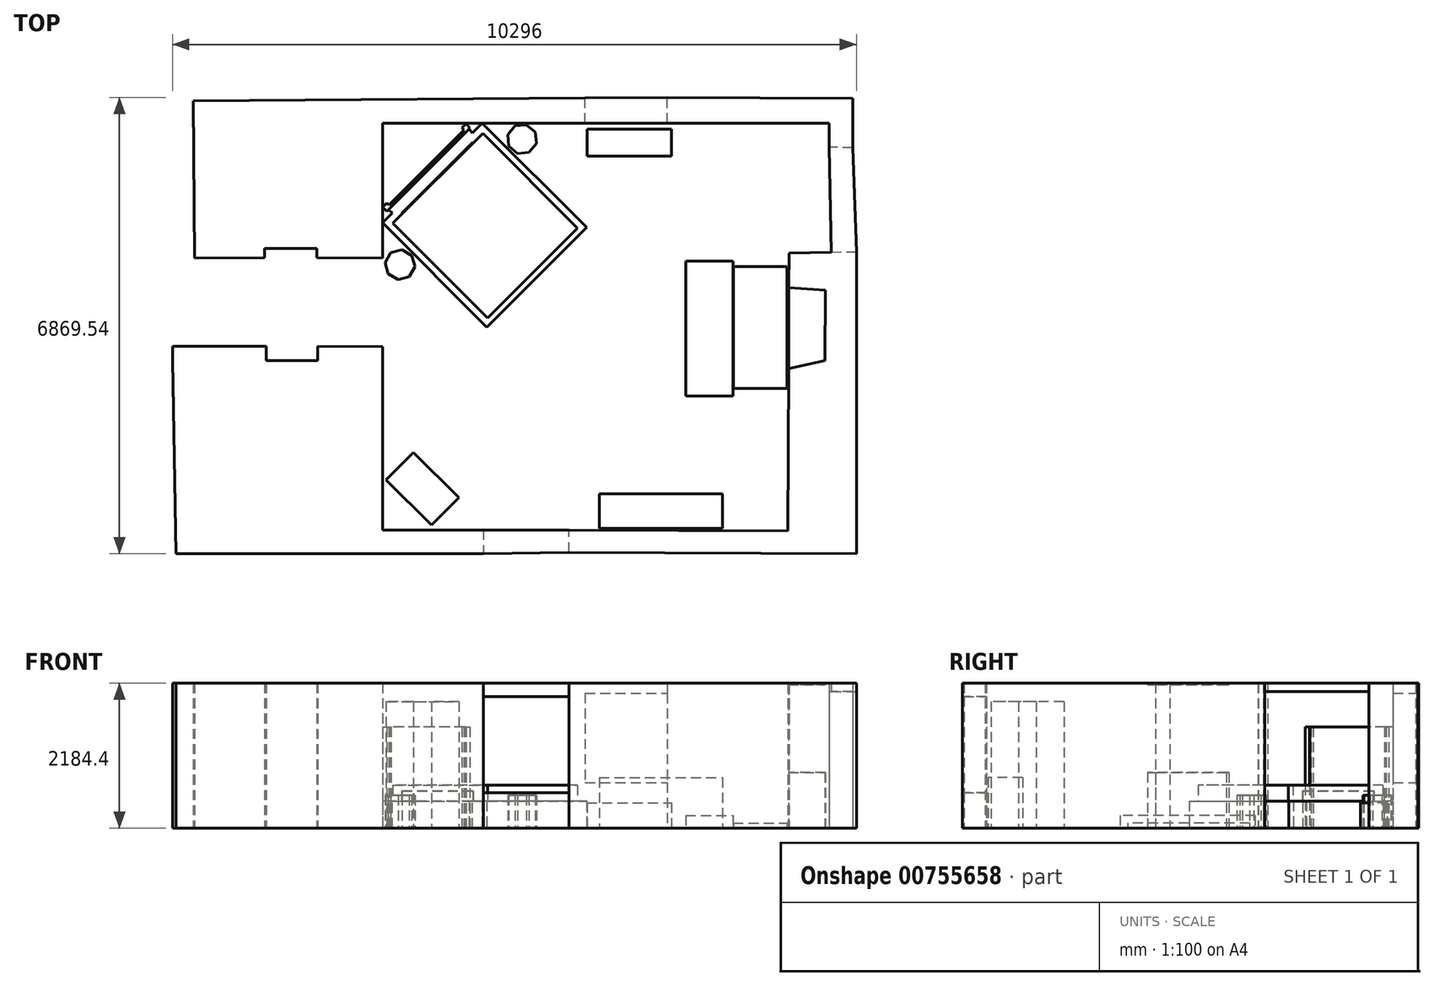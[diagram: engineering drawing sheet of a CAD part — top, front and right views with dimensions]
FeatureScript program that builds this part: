
annotation { "Feature Type Name" : "Feature", "Feature Type Description" : "" }
export const myFeature = defineFeature(function(context is Context, id is Id, definition is map)
    precondition{}
    {
        {
            var Q0;
            Q0=qCreatedBy(makeId("Top.planeOp"),FACE);
            var sketch = newSketch(context, id + "F0", { "sketchPlane" : qUnion([Q0])});
            skLineSegment(sketch, "E0", {"start": v(0, 0) * mm, "end": v(0, -2032) * mm});
            skLineSegment(sketch, "E1", {"start": v(0, 0) * mm, "end": v(3033.71, 0) * mm});
            skLineSegment(sketch, "E2", {"start": v(4288.2, 0) * mm, "end": v(6068.64, 0) * mm});
            skLineSegment(sketch, "E3", {"start": v(0, -2032) * mm, "end": v(0, -6124.58) * mm});
            skPoint(sketch, "E4", {"position": v(0, -1397) * mm});
            skPoint(sketch, "E5", {"position": v(1397, 0) * mm});
            skLineSegment(sketch, "E6", {"start": v(0, -1397) * mm, "end": v(1397, 0) * mm});
            skPoint(sketch, "E7", {"position": v(698.5, -698.5) * mm});
            skLineSegment(sketch, "E8", {"start": v(698.5, -698.5) * mm, "end": v(4954.33, -4954.33) * mm, "construction": true});
            skPoint(sketch, "E9", {"position": v(2270.04, -2270.04) * mm});
            skLineSegment(sketch, "E10", {"start": v(2270.04, -2270.04) * mm, "end": v(1520.2, -3019.9) * mm});
            skPoint(sketch, "E11", {"position": v(1663.88, -2876.21) * mm});
            skLineSegment(sketch, "E12", {"start": v(1571.54, -3071.25) * mm, "end": v(0, -1499.7) * mm});
            skLineSegment(sketch, "E13", {"start": v(1663.88, -2876.21) * mm, "end": v(92.33, -1304.67) * mm});
            skLineSegment(sketch, "E14", {"start": v(0, -1499.7) * mm, "end": v(749.85, -749.85) * mm});
            skLineSegment(sketch, "E15", {"start": v(1571.54, -3071.25) * mm, "end": v(2321.4, -2321.4) * mm});
            skLineSegment(sketch, "E16.MirrorCS", {"start": v(1397, 0) * mm, "end": v(0, -1397) * mm});
            skLineSegment(sketch, "E17.MirrorCS", {"start": v(2876.21, -1663.88) * mm, "end": v(1304.67, -92.33) * mm});
            skLineSegment(sketch, "E18.MirrorCS", {"start": v(2270.04, -2270.04) * mm, "end": v(3019.9, -1520.2) * mm});
            skLineSegment(sketch, "E19.MirrorCS", {"start": v(3071.25, -1571.54) * mm, "end": v(1499.7, 0) * mm});
            skLineSegment(sketch, "E20.MirrorCS", {"start": v(3071.25, -1571.54) * mm, "end": v(2321.4, -2321.4) * mm});
            skLineSegment(sketch, "E21.MirrorCS", {"start": v(1499.7, 0) * mm, "end": v(749.85, -749.85) * mm});
            skSolve(sketch);
        }
        {
            var Q0;
            {var subQ1=sQuery(id+"F0.wireOp",EDGE,"E16.MirrorCS");var subQ7=sQuery(id+"F0.wireOp",EDGE,"E13");var subQ9=makeQuery(id+"F0.imprint","INTERSECT",VERTEX,{"derivedFrom":[subQ7,subQ1]});Q0=makeQuery(id+"F0.imprint","IMPRINT",FACE,{"disambiguationData":[TD([[makeQuery(id+"F0.imprint","IMPRINT",EDGE,{"disambiguationData":[TD([[subQ9,1.0]])],"derivedFrom":subQ7}),-1.0]])]});}
            var Q1;
            {var subQ0=sQuery(id+"F0.wireOp",EDGE,"E18.MirrorCS");var subQ9=sQuery(id+"F0.wireOp",EDGE,"E10");var subQ11=makeQuery(id+"F0.imprint","INTERSECT",VERTEX,{"derivedFrom":[subQ9,subQ0]});Q1=makeQuery(id+"F0.imprint","IMPRINT",FACE,{"disambiguationData":[TD([[makeQuery(id+"F0.imprint","IMPRINT",EDGE,{"disambiguationData":[TD([[subQ11,-1.0]])],"derivedFrom":subQ9}),-1.0]])]});}
            extrude(context, id + "F1", {"entities" : qUnion([Q0, Q1]), "depth" : 406.4 * mm, "offsetDistance" : 25.4 * mm});
        }
        {
            var Q0;
            {var subQ0=sQuery(id+"F0.wireOp",EDGE,"E18.MirrorCS");var subQ9=sQuery(id+"F0.wireOp",EDGE,"E10");var subQ11=makeQuery(id+"F0.imprint","INTERSECT",VERTEX,{"derivedFrom":[subQ9,subQ0]});Q0=makeQuery(id+"F0.imprint","IMPRINT",FACE,{"disambiguationData":[TD([[makeQuery(id+"F0.imprint","IMPRINT",EDGE,{"disambiguationData":[TD([[subQ11,-1.0]])],"derivedFrom":subQ9}),-1.0]])]});}
            var Q1;
            {var subQ0=sQuery(id+"F0.wireOp",EDGE,"E12");var subQ1=sQuery(id+"F0.wireOp",EDGE,"E10");var subQ2=makeQuery(id+"F0.imprint","INTERSECT",VERTEX,{"derivedFrom":[subQ1,subQ0]});Q1=makeQuery(id+"F0.imprint","IMPRINT",FACE,{"disambiguationData":[TD([[makeQuery(id+"F0.imprint","IMPRINT",EDGE,{"disambiguationData":[TD([[subQ2,1.0]])],"derivedFrom":subQ1}),-1.0]])]});}
            var Q2;
            {var subQ0=sQuery(id+"F0.wireOp",EDGE,"E18.MirrorCS");var subQ1=sQuery(id+"F0.wireOp",EDGE,"E17.MirrorCS");var subQ2=makeQuery(id+"F0.imprint","INTERSECT",VERTEX,{"derivedFrom":[subQ1,subQ0]});Q2=makeQuery(id+"F0.imprint","IMPRINT",FACE,{"disambiguationData":[TD([[makeQuery(id+"F0.imprint","IMPRINT",EDGE,{"disambiguationData":[TD([[subQ2,-1.0]])],"derivedFrom":subQ1}),-1.0]])]});}
            var Q3;
            {var subQ0=sQuery(id+"F0.wireOp",EDGE,"E15");Q3=makeQuery(id+"F0.imprint","IMPRINT",FACE,{"disambiguationData":[TD([[makeQuery(id+"F0.imprint","IMPRINT",EDGE,{"derivedFrom":subQ0}),1.0]])]});}
            extrude(context, id + "F2", {"entities" : qUnion([Q0, Q1, Q2, Q3]), "depth" : 406.4 * mm, "offsetDistance" : 25.4 * mm});
        }
        {
            var Q0;
            Q0=qCreatedBy(makeId("Top.planeOp"),FACE);
            var sketch = newSketch(context, id + "F3", { "sketchPlane" : qUnion([Q0])});
            skLineSegment(sketch, "E22.0", {"start": v(0, -1397) * mm, "end": v(1397, 0) * mm, "construction": true});
            skLineSegment(sketch, "E23.0", {"start": v(2270.04, -2270.04) * mm, "end": v(1520.2, -3019.9) * mm, "construction": true});
            skLineSegment(sketch, "E24.0", {"start": v(698.5, -698.5) * mm, "end": v(4954.33, -4954.33) * mm, "construction": true});
            skPoint(sketch, "E25", {"position": v(824.22, -824.22) * mm});
            skPoint(sketch, "E26", {"position": v(2198.2, -2198.2) * mm});
            skLineSegment(sketch, "E27", {"start": v(2198.2, -2198.2) * mm, "end": v(1659.39, -2737.02) * mm});
            skLineSegment(sketch, "E28", {"start": v(285.94, -1362.51) * mm, "end": v(1659.39, -2737.02) * mm});
            skLineSegment(sketch, "E29.MirrorCS", {"start": v(1362.51, -285.94) * mm, "end": v(2737.02, -1659.39) * mm});
            skLineSegment(sketch, "E30.MirrorCS", {"start": v(2198.2, -2198.2) * mm, "end": v(2737.02, -1659.39) * mm});
            skLineSegment(sketch, "E31", {"start": v(1362.51, -285.94) * mm, "end": v(285.94, -1362.51) * mm});
            skPoint(sketch, "E32.orphan", {"position": v(261.91, -1338.47) * mm});
            skPoint(sketch, "E33.MirrorCS.end.orphan", {"position": v(1338.47, -261.91) * mm});
            skSolve(sketch);
        }
        {
            var Q0;
            Q0=makeQuery(id+"F3.imprint","IMPRINT",FACE,{"disambiguationData":[TD([[makeQuery(id+"F3.imprint","IMPRINT",EDGE,{"derivedFrom":sQuery(id+"F3.wireOp",EDGE,"E27")}),-1.0]])]});
            extrude(context, id + "F4", {"entities" : qUnion([Q0]), "operationType" : NewBodyOperationType.ADD, "depth" : 558.8 * mm, "offsetDistance" : 25.4 * mm});
        }
        {
            var Q0;
            Q0=qCreatedBy(makeId("Top.planeOp"),FACE);
            var sketch = newSketch(context, id + "F5", { "sketchPlane" : qUnion([Q0])});
            skLineSegment(sketch, "E34.0", {"start": v(0, -1499.7) * mm, "end": v(749.85, -749.85) * mm, "construction": true});
            skLineSegment(sketch, "E35.0", {"start": v(698.5, -698.5) * mm, "end": v(4954.33, -4954.33) * mm, "construction": true});
            skLineSegment(sketch, "E36.0", {"start": v(1571.54, -3071.25) * mm, "end": v(2321.4, -2321.4) * mm, "construction": true});
            skPoint(sketch, "E37", {"position": v(2258.53, -2258.53) * mm});
            skPoint(sketch, "E38", {"position": v(830.67, -830.67) * mm});
            skLineSegment(sketch, "E39", {"start": v(2258.53, -2258.53) * mm, "end": v(1580.53, -2936.54) * mm});
            skLineSegment(sketch, "E40", {"start": v(830.67, -830.67) * mm, "end": v(152.66, -1508.68) * mm});
            skLineSegment(sketch, "E41", {"start": v(152.66, -1508.68) * mm, "end": v(1580.53, -2936.54) * mm});
            skLineSegment(sketch, "E42.MirrorCS", {"start": v(830.67, -830.67) * mm, "end": v(1508.68, -152.66) * mm});
            skLineSegment(sketch, "E43.MirrorCS", {"start": v(1508.68, -152.66) * mm, "end": v(2936.54, -1580.53) * mm});
            skLineSegment(sketch, "E44.MirrorCS", {"start": v(2258.53, -2258.53) * mm, "end": v(2936.54, -1580.53) * mm});
            skSolve(sketch);
        }
        {
            var Q0;
            Q0 = qSketchRegion(id + "F5", true);
            extrude(context, id + "F6", {"entities" : qUnion([Q0]), "operationType" : NewBodyOperationType.ADD, "depth" : 647.7 * mm, "offsetDistance" : 25.4 * mm});
        }
        {
            var Q0;
            Q0=qCreatedBy(makeId("Top.planeOp"),FACE);
            var sketch = newSketch(context, id + "F7", { "sketchPlane" : qUnion([Q0])});
            skLineSegment(sketch, "E45", {"start": v(0, -2032.3) * mm, "end": v(0, 0) * mm});
            skLineSegment(sketch, "E46", {"start": v(0, 0) * mm, "end": v(3048.77, 0) * mm});
            skLineSegment(sketch, "E47", {"start": v(3048.77, 0) * mm, "end": v(3048.77, 378.32) * mm});
            skLineSegment(sketch, "E48", {"start": v(3048.77, 378.32) * mm, "end": v(-2849.77, 339.02) * mm});
            skLineSegment(sketch, "E49", {"start": v(-2849.77, 339.02) * mm, "end": v(-2833.96, -2034.52) * mm});
            skLineSegment(sketch, "E50", {"start": v(-2833.96, -2034.52) * mm, "end": v(-1776.95, -2027.47) * mm});
            skLineSegment(sketch, "E51", {"start": v(-1776.95, -2027.47) * mm, "end": v(-1776.95, -1886.84) * mm});
            skLineSegment(sketch, "E52", {"start": v(-1776.95, -1886.84) * mm, "end": v(-988.05, -1886.84) * mm});
            skLineSegment(sketch, "E53", {"start": v(-988.05, -1886.84) * mm, "end": v(-988.05, -2027.47) * mm});
            skLineSegment(sketch, "E54", {"start": v(-988.05, -2027.47) * mm, "end": v(0, -2032.3) * mm});
            skLineSegment(sketch, "E55", {"start": v(-977.96, -3360.01) * mm, "end": v(0, -3364.8) * mm});
            skLineSegment(sketch, "E56", {"start": v(0, -3364.8) * mm, "end": v(0, -6126.67) * mm});
            skLineSegment(sketch, "E57", {"start": v(0, -6126.67) * mm, "end": v(1516.33, -6126.67) * mm});
            skLineSegment(sketch, "E58", {"start": v(1516.33, -6126.67) * mm, "end": v(1516.33, -6483.37) * mm});
            skLineSegment(sketch, "E59", {"start": v(1516.33, -6483.37) * mm, "end": v(-977.96, -6483.37) * mm});
            skLineSegment(sketch, "E60", {"start": v(-977.96, -3578) * mm, "end": v(-977.96, -3360.01) * mm});
            skLineSegment(sketch, "E61", {"start": v(2807.64, -6126.67) * mm, "end": v(6104.66, -6142.79) * mm});
            skLineSegment(sketch, "E62", {"start": v(6104.66, -6142.79) * mm, "end": v(6116.6, -3699.37) * mm});
            skLineSegment(sketch, "E63", {"start": v(6116.6, -3699.37) * mm, "end": v(6663.05, -3578.6) * mm});
            skLineSegment(sketch, "E64", {"start": v(6663.05, -3578.6) * mm, "end": v(6668.26, -2512.91) * mm});
            skLineSegment(sketch, "E65", {"start": v(6668.26, -2512.91) * mm, "end": v(6116.6, -2475.3) * mm});
            skLineSegment(sketch, "E66", {"start": v(6116.6, -2475.3) * mm, "end": v(6119.15, -1954.11) * mm});
            skLineSegment(sketch, "E67", {"start": v(6119.15, -1954.11) * mm, "end": v(7134.83, -1934.8) * mm});
            skLineSegment(sketch, "E68", {"start": v(7134.83, -1934.8) * mm, "end": v(7134.83, -6483.37) * mm});
            skLineSegment(sketch, "E69", {"start": v(7134.83, -6483.37) * mm, "end": v(2807.64, -6462.21) * mm});
            skLineSegment(sketch, "E70", {"start": v(2807.64, -6462.21) * mm, "end": v(2807.64, -6126.67) * mm});
            skLineSegment(sketch, "E71", {"start": v(4285.22, 0) * mm, "end": v(4285.22, 386.17) * mm});
            skLineSegment(sketch, "E72", {"start": v(4285.22, 386.17) * mm, "end": v(7080.61, 372.5) * mm});
            skLineSegment(sketch, "E73", {"start": v(7080.61, 372.5) * mm, "end": v(7080.61, -366.87) * mm});
            skLineSegment(sketch, "E74", {"start": v(7080.61, -366.87) * mm, "end": v(6727.83, -365.14) * mm});
            skLineSegment(sketch, "E75", {"start": v(6727.83, -365.14) * mm, "end": v(6727.83, 0) * mm});
            skLineSegment(sketch, "E76", {"start": v(6727.83, 0) * mm, "end": v(4285.22, 0) * mm});
            skLineSegment(sketch, "E77", {"start": v(3048.77, 378.32) * mm, "end": v(4285.22, 386.17) * mm});
            skLineSegment(sketch, "E78", {"start": v(3048.77, 0) * mm, "end": v(4285.22, 0) * mm});
            skLineSegment(sketch, "E79", {"start": v(1516.33, -6126.67) * mm, "end": v(2807.64, -6126.67) * mm});
            skLineSegment(sketch, "E80", {"start": v(1516.33, -6483.37) * mm, "end": v(2807.64, -6462.21) * mm});
            skLineSegment(sketch, "E81", {"start": v(7080.61, -366.87) * mm, "end": v(7134.83, -1934.8) * mm});
            skLineSegment(sketch, "E82", {"start": v(6727.83, -365.14) * mm, "end": v(6757.8, -1941.97) * mm});
            skPoint(sketch, "E83.orphan", {"position": v(6757.66, -1934.8) * mm});
            skLineSegment(sketch, "E84", {"start": v(6116.6, -2475.3) * mm, "end": v(6116.6, -3699.37) * mm});
            skLineSegment(sketch, "E85", {"start": v(-977.96, -3578) * mm, "end": v(-1751.08, -3578) * mm});
            skLineSegment(sketch, "E86", {"start": v(-3161.21, -3578) * mm, "end": v(-3161.21, -3360.01) * mm});
            skLineSegment(sketch, "E87", {"start": v(-3161.21, -3360.01) * mm, "end": v(-1751.08, -3360.01) * mm});
            skLineSegment(sketch, "E88", {"start": v(-1751.08, -3360.01) * mm, "end": v(-1751.08, -3578) * mm});
            skLineSegment(sketch, "E89", {"start": v(-3161.21, -3578) * mm, "end": v(-3113.41, -6483.37) * mm});
            skLineSegment(sketch, "E90", {"start": v(-3113.41, -6483.37) * mm, "end": v(-977.96, -6483.37) * mm});
            skSolve(sketch);
        }
        {
            var Q0;
            Q0=makeQuery(id+"F7.imprint","IMPRINT",FACE,{"disambiguationData":[TD([[makeQuery(id+"F7.imprint","IMPRINT",EDGE,{"derivedFrom":sQuery(id+"F7.wireOp",EDGE,"E45")}),1.0]])]});
            var Q1;
            Q1=makeQuery(id+"F7.imprint","IMPRINT",FACE,{"disambiguationData":[TD([[makeQuery(id+"F7.imprint","IMPRINT",EDGE,{"derivedFrom":sQuery(id+"F7.wireOp",EDGE,"E47")}),-1.0]])]});
            var Q2;
            Q2=makeQuery(id+"F7.imprint","IMPRINT",FACE,{"disambiguationData":[TD([[makeQuery(id+"F7.imprint","IMPRINT",EDGE,{"derivedFrom":sQuery(id+"F7.wireOp",EDGE,"E71")}),-1.0]])]});
            var Q3;
            Q3=makeQuery(id+"F7.imprint","IMPRINT",FACE,{"disambiguationData":[TD([[makeQuery(id+"F7.imprint","IMPRINT",EDGE,{"derivedFrom":sQuery(id+"F7.wireOp",EDGE,"E74")}),1.0]])]});
            var Q4;
            Q4=makeQuery(id+"F7.imprint","IMPRINT",FACE,{"disambiguationData":[TD([[makeQuery(id+"F7.imprint","IMPRINT",EDGE,{"derivedFrom":sQuery(id+"F7.wireOp",EDGE,"E61")}),-1.0]])]});
            var Q5;
            Q5=makeQuery(id+"F7.imprint","IMPRINT",FACE,{"disambiguationData":[TD([[makeQuery(id+"F7.imprint","IMPRINT",EDGE,{"derivedFrom":sQuery(id+"F7.wireOp",EDGE,"E58")}),1.0]])]});
            var Q6;
            Q6=makeQuery(id+"F7.imprint","IMPRINT",FACE,{"disambiguationData":[TD([[makeQuery(id+"F7.imprint","IMPRINT",EDGE,{"derivedFrom":sQuery(id+"F7.wireOp",EDGE,"E55")}),-1.0]])]});
            extrude(context, id + "F8", {"entities" : qUnion([Q0, Q1, Q2, Q3, Q4, Q5, Q6]), "depth" : 2184.4 * mm, "offsetDistance" : 25.4 * mm});
        }
        {
            var Q0;
            Q0=makeQuery(id+"F7.imprint","IMPRINT",FACE,{"disambiguationData":[TD([[makeQuery(id+"F7.imprint","IMPRINT",EDGE,{"derivedFrom":sQuery(id+"F7.wireOp",EDGE,"E47")}),-1.0]])]});
            extrude(context, id + "F9", {"entities" : qUnion([Q0]), "operationType" : NewBodyOperationType.REMOVE, "depth" : 2032 * mm, "offsetDistance" : 25.4 * mm, "hasSecondDirection" : true, "secondDirectionOppositeDirection" : false, "secondDirectionDepth" : 685.8 * mm});
        }
        {
            var Q0;
            Q0=makeQuery(id+"F7.imprint","IMPRINT",FACE,{"disambiguationData":[TD([[makeQuery(id+"F7.imprint","IMPRINT",EDGE,{"derivedFrom":sQuery(id+"F7.wireOp",EDGE,"E74")}),1.0]])]});
            extrude(context, id + "F10", {"entities" : qUnion([Q0]), "operationType" : NewBodyOperationType.REMOVE, "depth" : 2057.4 * mm, "offsetDistance" : 25.4 * mm});
        }
        {
            var Q0;
            Q0=makeQuery(id+"F7.imprint","IMPRINT",FACE,{"disambiguationData":[TD([[makeQuery(id+"F7.imprint","IMPRINT",EDGE,{"derivedFrom":sQuery(id+"F7.wireOp",EDGE,"E58")}),1.0]])]});
            extrude(context, id + "F11", {"entities" : qUnion([Q0]), "operationType" : NewBodyOperationType.REMOVE, "depth" : 1981.2 * mm, "offsetDistance" : 25.4 * mm, "hasSecondDirection" : true, "secondDirectionOppositeDirection" : false, "secondDirectionDepth" : 533.4 * mm});
        }
        {
            var Q0;
            Q0=makeQuery(id+"F7.imprint","IMPRINT",FACE,{"disambiguationData":[TD([[makeQuery(id+"F7.imprint","IMPRINT",EDGE,{"derivedFrom":sQuery(id+"F7.wireOp",EDGE,"E63")}),1.0]])]});
            extrude(context, id + "F12", {"entities" : qUnion([Q0]), "operationType" : NewBodyOperationType.ADD, "depth" : 2159 * mm, "offsetDistance" : 25.4 * mm, "hasSecondDirection" : true, "secondDirectionOppositeDirection" : false, "secondDirectionDepth" : 838.2 * mm});
        }
        {
            var Q0;
            Q0=qCreatedBy(makeId("Top.planeOp"),FACE);
            var sketch = newSketch(context, id + "F13", { "sketchPlane" : qUnion([Q0])});
            skLineSegment(sketch, "E91.bottom", {"start": v(5282.23, -2160.48) * mm, "end": v(6093.22, -2160.48) * mm});
            skLineSegment(sketch, "E91.top", {"start": v(5282.23, -3995.76) * mm, "end": v(6093.22, -3995.76) * mm});
            skLineSegment(sketch, "E91.left", {"start": v(5282.23, -2160.48) * mm, "end": v(5282.23, -3995.76) * mm});
            skLineSegment(sketch, "E91.right", {"start": v(6093.22, -2160.48) * mm, "end": v(6093.22, -3995.76) * mm});
            skLineSegment(sketch, "E92.bottom", {"start": v(4565.25, -2077.81) * mm, "end": v(5276.45, -2077.81) * mm});
            skLineSegment(sketch, "E92.top", {"start": v(4565.25, -4109.81) * mm, "end": v(5276.45, -4109.81) * mm});
            skLineSegment(sketch, "E92.left", {"start": v(4565.25, -2077.81) * mm, "end": v(4565.25, -4109.81) * mm});
            skLineSegment(sketch, "E92.right", {"start": v(5276.45, -2077.81) * mm, "end": v(5276.45, -4109.81) * mm});
            skPoint(sketch, "E93", {"position": v(5276.45, -3093.81) * mm});
            skPoint(sketch, "E94", {"position": v(5282.23, -3078.12) * mm});
            skLineSegment(sketch, "E95.bottom", {"start": v(3077.3, -87.2) * mm, "end": v(4347.3, -87.2) * mm});
            skLineSegment(sketch, "E95.top", {"start": v(3077.3, -493.6) * mm, "end": v(4347.3, -493.6) * mm});
            skLineSegment(sketch, "E95.left", {"start": v(3077.3, -87.2) * mm, "end": v(3077.3, -493.6) * mm});
            skLineSegment(sketch, "E95.right", {"start": v(4347.3, -87.2) * mm, "end": v(4347.3, -493.6) * mm});
            skLineSegment(sketch, "E96.bottom", {"start": v(466.54, -4959.25) * mm, "end": v(1149.04, -5641.75) * mm});
            skLineSegment(sketch, "E96.top", {"start": v(53.45, -5372.34) * mm, "end": v(735.95, -6054.84) * mm});
            skLineSegment(sketch, "E96.left", {"start": v(466.54, -4959.25) * mm, "end": v(53.45, -5372.34) * mm});
            skLineSegment(sketch, "E96.right", {"start": v(1149.04, -5641.75) * mm, "end": v(735.95, -6054.84) * mm});
            skLineSegment(sketch, "E97.bottom", {"start": v(3262.98, -5580.22) * mm, "end": v(5117.18, -5580.22) * mm});
            skLineSegment(sketch, "E97.top", {"start": v(3262.98, -6100.92) * mm, "end": v(5117.18, -6100.92) * mm});
            skLineSegment(sketch, "E97.left", {"start": v(3262.98, -5580.22) * mm, "end": v(3262.98, -6100.92) * mm});
            skLineSegment(sketch, "E97.right", {"start": v(5117.18, -5580.22) * mm, "end": v(5117.18, -6100.92) * mm});
            skCircle(sketch, "E98.cCircle", {"center": v(261.66, -2130.17) * mm, "radius": 209.55 * mm, "construction": true});
            skLineSegment(sketch, "E98.0", {"start": v(486.6, -2159.2) * mm, "end": v(400.2, -2309.76) * mm});
            skLineSegment(sketch, "E98.1", {"start": v(400.2, -2309.76) * mm, "end": v(232.63, -2355.12) * mm});
            skLineSegment(sketch, "E98.2", {"start": v(232.63, -2355.12) * mm, "end": v(82.07, -2268.71) * mm});
            skLineSegment(sketch, "E98.3", {"start": v(82.07, -2268.71) * mm, "end": v(36.7, -2101.14) * mm});
            skLineSegment(sketch, "E98.4", {"start": v(36.7, -2101.14) * mm, "end": v(123.12, -1950.58) * mm});
            skLineSegment(sketch, "E98.5", {"start": v(123.12, -1950.58) * mm, "end": v(290.69, -1905.22) * mm});
            skLineSegment(sketch, "E98.6", {"start": v(290.69, -1905.22) * mm, "end": v(441.25, -1991.64) * mm});
            skLineSegment(sketch, "E98.7", {"start": v(441.25, -1991.64) * mm, "end": v(486.6, -2159.2) * mm});
            skPoint(sketch, "E98.0.midPoint", {"position": v(443.4, -2234.48) * mm});
            skCircle(sketch, "E99.cCircle", {"center": v(2100.01, -239.15) * mm, "radius": 209.55 * mm, "construction": true});
            skLineSegment(sketch, "E99.0", {"start": v(2316.22, -307.7) * mm, "end": v(2204.42, -440.5) * mm});
            skLineSegment(sketch, "E99.1", {"start": v(2204.42, -440.5) * mm, "end": v(2031.46, -455.35) * mm});
            skLineSegment(sketch, "E99.2", {"start": v(2031.46, -455.35) * mm, "end": v(1898.66, -343.55) * mm});
            skLineSegment(sketch, "E99.3", {"start": v(1898.66, -343.55) * mm, "end": v(1883.8, -170.59) * mm});
            skLineSegment(sketch, "E99.4", {"start": v(1883.8, -170.59) * mm, "end": v(1995.6, -37.79) * mm});
            skLineSegment(sketch, "E99.5", {"start": v(1995.6, -37.79) * mm, "end": v(2168.57, -22.94) * mm});
            skLineSegment(sketch, "E99.6", {"start": v(2168.57, -22.94) * mm, "end": v(2301.37, -134.74) * mm});
            skLineSegment(sketch, "E99.7", {"start": v(2301.37, -134.74) * mm, "end": v(2316.22, -307.7) * mm});
            skPoint(sketch, "E99.0.midPoint", {"position": v(2260.32, -374.1) * mm});
            skSolve(sketch);
        }
        {
            var Q0;
            Q0=makeQuery(id+"F13.imprint","IMPRINT",FACE,{"disambiguationData":[TD([[makeQuery(id+"F13.imprint","IMPRINT",EDGE,{"derivedFrom":sQuery(id+"F13.wireOp",EDGE,"E99.0")}),-1.0]])]});
            var Q1;
            Q1=makeQuery(id+"F13.imprint","IMPRINT",FACE,{"disambiguationData":[TD([[makeQuery(id+"F13.imprint","IMPRINT",EDGE,{"derivedFrom":sQuery(id+"F13.wireOp",EDGE,"E98.0")}),-1.0]])]});
            extrude(context, id + "F14", {"entities" : qUnion([Q0, Q1]), "depth" : 495.3 * mm, "offsetDistance" : 25.4 * mm});
        }
        {
            var Q0;
            Q0=makeQuery(id+"F13.imprint","IMPRINT",FACE,{"disambiguationData":[TD([[makeQuery(id+"F13.imprint","IMPRINT",EDGE,{"derivedFrom":sQuery(id+"F13.wireOp",EDGE,"E95.bottom")}),-1.0]])]});
            extrude(context, id + "F15", {"entities" : qUnion([Q0]), "depth" : 381 * mm, "offsetDistance" : 25.4 * mm});
        }
        {
            var Q0;
            Q0=makeQuery(id+"F13.imprint","IMPRINT",FACE,{"disambiguationData":[TD([[makeQuery(id+"F13.imprint","IMPRINT",EDGE,{"derivedFrom":sQuery(id+"F13.wireOp",EDGE,"E91.bottom")}),-1.0]])]});
            extrude(context, id + "F16", {"entities" : qUnion([Q0]), "depth" : 76.2 * mm, "offsetDistance" : 25.4 * mm});
        }
        {
            var Q0;
            Q0=makeQuery(id+"F13.imprint","IMPRINT",FACE,{"disambiguationData":[TD([[makeQuery(id+"F13.imprint","IMPRINT",EDGE,{"derivedFrom":sQuery(id+"F13.wireOp",EDGE,"E92.bottom")}),-1.0]])]});
            extrude(context, id + "F17", {"entities" : qUnion([Q0]), "depth" : 190.5 * mm, "offsetDistance" : 25.4 * mm});
        }
        {
            var Q0;
            Q0=makeQuery(id+"F13.imprint","IMPRINT",FACE,{"disambiguationData":[TD([[makeQuery(id+"F13.imprint","IMPRINT",EDGE,{"derivedFrom":sQuery(id+"F13.wireOp",EDGE,"E96.bottom")}),-1.0]])]});
            extrude(context, id + "F18", {"entities" : qUnion([Q0]), "depth" : 1905 * mm, "offsetDistance" : 25.4 * mm});
        }
        {
            var Q0;
            Q0=makeQuery(id+"F13.imprint","IMPRINT",FACE,{"disambiguationData":[TD([[makeQuery(id+"F13.imprint","IMPRINT",EDGE,{"derivedFrom":sQuery(id+"F13.wireOp",EDGE,"E97.bottom")}),-1.0]])]});
            extrude(context, id + "F19", {"entities" : qUnion([Q0]), "depth" : 762 * mm, "offsetDistance" : 25.4 * mm});
        }
        {
            var Q0;
            Q0=qCreatedBy(makeId("Top.planeOp"),FACE);
            var sketch = newSketch(context, id + "F20", { "sketchPlane" : qUnion([Q0])});
            skLineSegment(sketch, "E100.bottom", {"start": v(1.8, -1262.92) * mm, "end": v(64.66, -1200.06) * mm});
            skLineSegment(sketch, "E100.top", {"start": v(64.66, -1325.78) * mm, "end": v(127.52, -1262.92) * mm});
            skLineSegment(sketch, "E100.left", {"start": v(1.8, -1262.92) * mm, "end": v(64.66, -1325.78) * mm});
            skLineSegment(sketch, "E100.right", {"start": v(64.66, -1200.06) * mm, "end": v(127.52, -1262.92) * mm});
            skLineSegment(sketch, "E101.bottom", {"start": v(1192.32, -68.1) * mm, "end": v(1255.18, -5.23) * mm});
            skLineSegment(sketch, "E101.top", {"start": v(1255.18, -130.96) * mm, "end": v(1318.04, -68.1) * mm});
            skLineSegment(sketch, "E101.left", {"start": v(1192.32, -68.1) * mm, "end": v(1255.18, -130.96) * mm});
            skLineSegment(sketch, "E101.right", {"start": v(1255.18, -5.23) * mm, "end": v(1318.04, -68.1) * mm});
            skPoint(sketch, "E102", {"position": v(1246.2, -121.98) * mm});
            skPoint(sketch, "E103", {"position": v(1228.24, -104.02) * mm});
            skLineSegment(sketch, "E104", {"start": v(1246.2, -121.98) * mm, "end": v(116.4, -1251.79) * mm});
            skLineSegment(sketch, "E105", {"start": v(1228.24, -104.02) * mm, "end": v(98.43, -1233.83) * mm});
            skSolve(sketch);
        }
        {
            var Q0;
            Q0 = qSketchRegion(id + "F20", true);
            extrude(context, id + "F21", {"entities" : qUnion([Q0]), "depth" : 1524 * mm, "offsetDistance" : 25.4 * mm});
        }
    });
